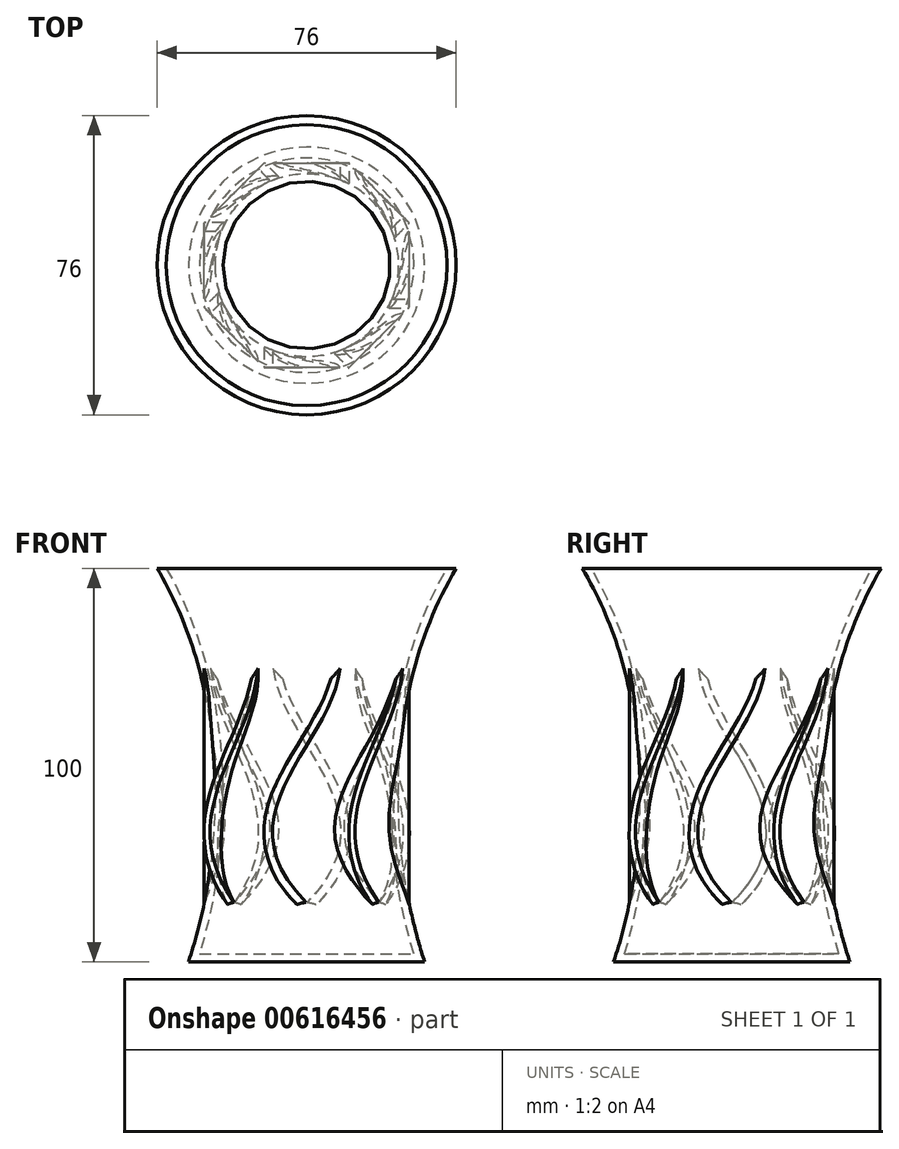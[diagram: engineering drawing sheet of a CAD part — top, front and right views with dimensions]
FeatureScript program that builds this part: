
annotation { "Feature Type Name" : "Feature", "Feature Type Description" : "" }
export const myFeature = defineFeature(function(context is Context, id is Id, definition is map)
    precondition{}
    {
        {
            var Q0;
            Q0=qCreatedBy(makeId("Front.planeOp"),FACE);
            var sketch = newSketch(context, id + "F0", { "sketchPlane" : qUnion([Q0])});
            skLineSegment(sketch, "E0", {"start": v(0, 0) * mm, "end": v(-30, 0) * mm});
            skLineSegment(sketch, "E1", {"start": v(0, 0) * mm, "end": v(0, 100) * mm});
            skLineSegment(sketch, "E2", {"start": v(0, 100) * mm, "end": v(-38, 100) * mm});
            skFitSpline(sketch, "E3", {"points": [v(-38, 100) * mm, v(-30, 0) * mm], "startDerivative": vector(54, -90) * mm, "endDerivative": vector(-30, -90) * mm});
            skSolve(sketch);
        }
        {
            var Q0;
            Q0=makeQuery(id+"F0.imprint","IMPRINT",FACE,{"disambiguationData":[TD([[makeQuery(id+"F0.imprint","IMPRINT",EDGE,{"derivedFrom":sQuery(id+"F0.wireOp",EDGE,"E0")}),-1.0]])]});
            var Q1;
            Q1=sQuery(id+"F0.wireOp",EDGE,"E1");
            revolve(context, id + "F1", {"entities" : qUnion([Q0]), "axis" : qUnion([Q1]), "revolveType" : RevolveType.FULL});
        }
        {
            var Q0;
            Q0=qCreatedBy(makeId("Front.planeOp"),FACE);
            var sketch = newSketch(context, id + "F2", { "sketchPlane" : qUnion([Q0])});
            skFitSpline(sketch, "E4", {"points": [v(0, 95) * mm, v(0, 55) * mm, v(0, 15) * mm], "startDerivative": vector(90, -90) * mm, "endDerivative": vector(90, -90) * mm});
            skFitSpline(sketch, "E5.0", {"points": [v(-1.41, 93.59) * mm, v(0.38, 91.79) * mm, v(3.26, 88.31) * mm, v(5.75, 83.44) * mm, v(6.77, 78.84) * mm, v(6.62, 74.35) * mm, v(5.49, 69.84) * mm, v(3.56, 65.29) * mm, v(1.08, 60.7) * mm, v(-1.7, 56.04) * mm, v(-4.54, 51.32) * mm, v(-7.16, 46.48) * mm, v(-9.28, 41.48) * mm, v(-10.6, 36.26) * mm, v(-10.8, 30.8) * mm, v(-9.54, 25.14) * mm, v(-6.58, 19.4) * mm, v(-3.37, 15.54) * mm, v(-1.41, 13.59) * mm]});
            skLineSegment(sketch, "E6", {"start": v(-1.41, 93.59) * mm, "end": v(0, 95) * mm});
            skLineSegment(sketch, "E7", {"start": v(-1.49, 13.66) * mm, "end": v(0, 15) * mm});
            skSolve(sketch);
        }
        {
            var Q0;
            Q0 = qSketchRegion(id + "F2", true);
            extrude(context, id + "F3", {"entities" : qUnion([Q0]), "operationType" : NewBodyOperationType.ADD, "depth" : 26 * mm, "offsetDistance" : 25 * mm});
        }
        {
            var Q0;
            Q0=makeQuery(id+"F1.opRevolve","SWEPT_BODY",BODY,{"disambiguationData":[OSD([sQuery(id+"F0.wireOp",EDGE,"E0"),sQuery(id+"F0.wireOp",EDGE,"E1"),sQuery(id+"F0.wireOp",EDGE,"E2"),sQuery(id+"F0.wireOp",EDGE,"E3")])]});
            var Q1;
            Q1=sQuery(id+"F0.wireOp",EDGE,"E1");
            circularPattern(context, id + "F4", {"operationType" : NewBodyOperationType.ADD, "entities" : qUnion([Q0]), "axis" : qUnion([Q1]), "angle" : 360 * degree, "instanceCount" : 8, "equalSpace" : true});
        }
        {
            var Q0;
            Q0=makeQuery(id+"F1.opRevolve","SWEPT_FACE",FACE,{"disambiguationData":[OSD([sQuery(id+"F0.wireOp",EDGE,"E2")])]});
            shell(context, id + "F5", {"entities" : qUnion([Q0]), "thickness" : 2 * mm});
        }
    });
